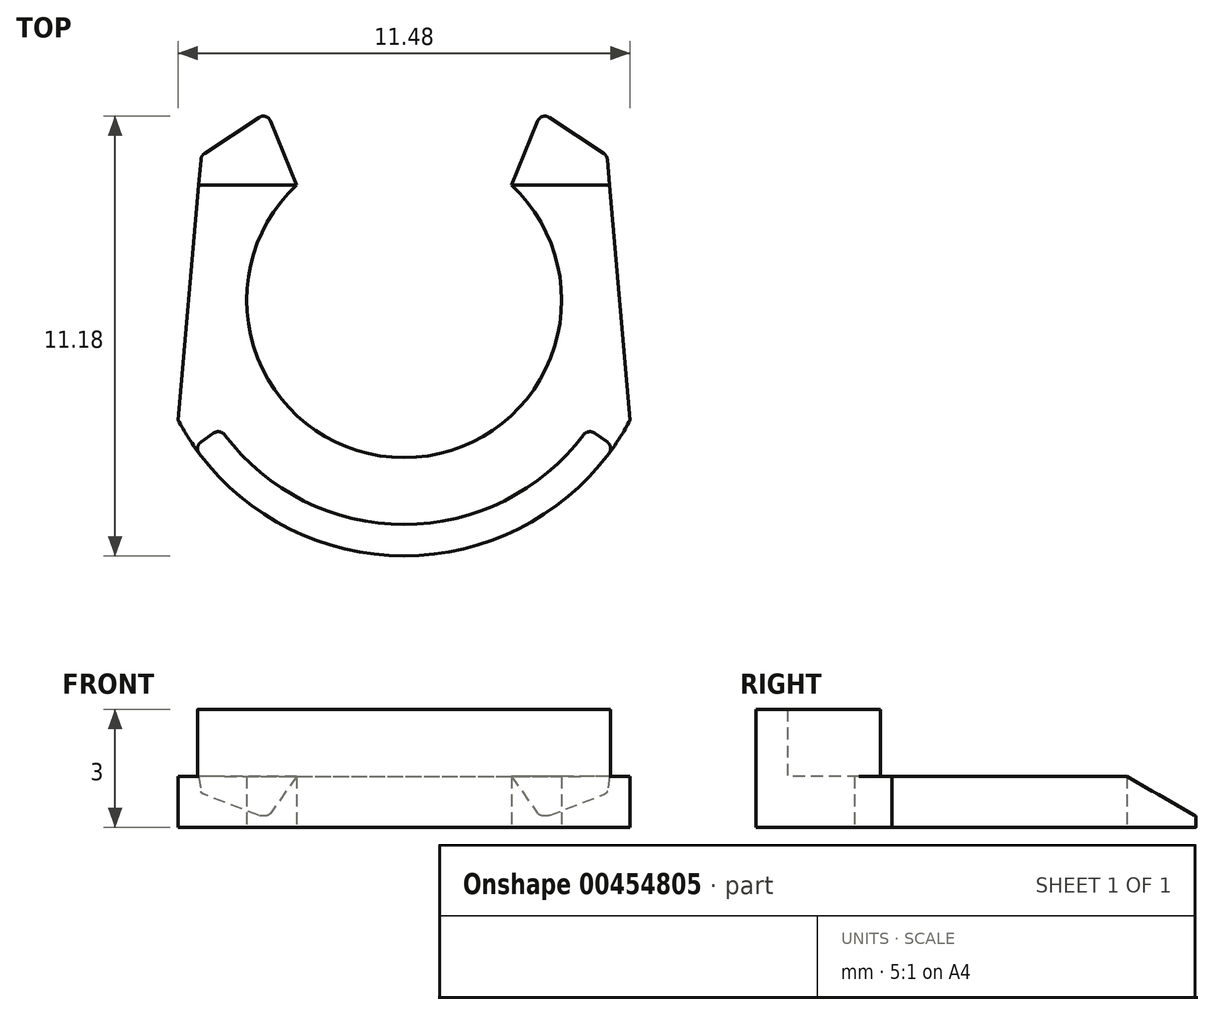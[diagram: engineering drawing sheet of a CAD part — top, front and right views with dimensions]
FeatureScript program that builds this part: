
annotation { "Feature Type Name" : "Feature", "Feature Type Description" : "" }
export const myFeature = defineFeature(function(context is Context, id is Id, definition is map)
    precondition{}
    {
        {
            assignVariable(context, id + "F0", {"name" : "thickness", "anyValue" : 1.3});
        }
        {
            var Q0;
            Q0=qCreatedBy(makeId("Top.planeOp"),FACE);
            var sketch = newSketch(context, id + "F1", { "sketchPlane" : qUnion([Q0])});
            skLineSegment(sketch, "E0.bottom", {"start": v(6, -6) * mm, "end": v(-6, -6) * mm, "construction": true});
            skLineSegment(sketch, "E0.top", {"start": v(4.95, 6) * mm, "end": v(-4.95, 6) * mm, "construction": true});
            skLineSegment(sketch, "E0.left", {"start": v(6, -6) * mm, "end": v(5.74, -3.05) * mm, "construction": true});
            skLineSegment(sketch, "E0.right", {"start": v(-6, -6) * mm, "end": v(-5.74, -3.05) * mm, "construction": true});
            skPoint(sketch, "E0.middle", {"position": v(0, 0) * mm});
            skPoint(sketch, "E1", {"position": v(0, 6) * mm});
            skPoint(sketch, "E2", {"position": v(0, -6) * mm});
            skLineSegment(sketch, "E3", {"start": v(0, 6) * mm, "end": v(0, -6) * mm, "construction": true});
            skLineSegment(sketch, "E4", {"start": v(-5.74, -3.05) * mm, "end": v(-5.15, 3.67) * mm});
            skLineSegment(sketch, "E5", {"start": v(5.74, -3.05) * mm, "end": v(5.15, 3.67) * mm});
            skArc(sketch, "E6", {"start": v(5.74, -3.05) * mm, "mid": v(0, 6.5) * mm, "end": v(-5.74, -3.05) * mm, "construction": true});
            skArc(sketch, "E7", {"start": v(-5.74, -3.05) * mm, "mid": v(0, -6.5) * mm, "end": v(5.74, -3.05) * mm});
            skLineSegment(sketch, "E8", {"start": v(2.73, 2.93) * mm, "end": v(3.49, 4.78) * mm});
            skLineSegment(sketch, "E9", {"start": v(3.49, 4.78) * mm, "end": v(5.15, 3.67) * mm});
            skLineSegment(sketch, "E10", {"start": v(-2.73, 2.93) * mm, "end": v(-3.49, 4.78) * mm});
            skLineSegment(sketch, "E11", {"start": v(-3.49, 4.78) * mm, "end": v(-5.15, 3.67) * mm});
            skLineSegment(sketch, "E12", {"start": v(-5.15, 3.67) * mm, "end": v(-4.95, 6) * mm, "construction": true});
            skLineSegment(sketch, "E13", {"start": v(5.15, 3.67) * mm, "end": v(4.95, 6) * mm, "construction": true});
            skArc(sketch, "E14", {"start": v(2.73, 2.93) * mm, "mid": v(0, 4) * mm, "end": v(-2.73, 2.93) * mm, "construction": true});
            skArc(sketch, "E15", {"start": v(-2.73, 2.93) * mm, "mid": v(0, -4) * mm, "end": v(2.73, 2.93) * mm});
            skSolve(sketch);
        }
        {
            var Q0;
            Q0 = qSketchRegion(id + "F1", true);
            extrude(context, id + "F2", {"entities" : qUnion([Q0]), "depth" : (getVariable(context, 'thickness')) * mm});
        }
        {
            var Q0;
            Q0=makeQuery(id+"F2.opExtrude","CAP_FACE",FACE,{"disambiguationData":[OSD([sQuery(id+"F1.wireOp",EDGE,"E4"),sQuery(id+"F1.wireOp",EDGE,"E5"),sQuery(id+"F1.wireOp",EDGE,"E7"),sQuery(id+"F1.wireOp",EDGE,"E8"),sQuery(id+"F1.wireOp",EDGE,"E9"),sQuery(id+"F1.wireOp",EDGE,"E10"),sQuery(id+"F1.wireOp",EDGE,"E11"),sQuery(id+"F1.wireOp",EDGE,"E15")])],"isStart":false});
            var sketch = newSketch(context, id + "F3", { "sketchPlane" : qUnion([Q0])});
            skArc(sketch, "E16.0", {"start": v(-5.33, -3.72) * mm, "mid": v(0, -6.5) * mm, "end": v(5.33, -3.72) * mm});
            skArc(sketch, "E17", {"start": v(-4.67, -3.27) * mm, "mid": v(0, -5.7) * mm, "end": v(4.67, -3.27) * mm});
            skLineSegment(sketch, "E18", {"start": v(0, 0) * mm, "end": v(-4.67, -3.27) * mm, "construction": true});
            skLineSegment(sketch, "E19", {"start": v(-9.02, -6.3) * mm, "end": v(9.02, -6.3) * mm, "construction": true});
            skLineSegment(sketch, "E20", {"start": v(9.02, -6.3) * mm, "end": v(5.33, -3.72) * mm, "construction": true});
            skLineSegment(sketch, "E21", {"start": v(0, -6.3) * mm, "end": v(0, 0) * mm, "construction": true});
            skLineSegment(sketch, "E22", {"start": v(-5.33, -3.72) * mm, "end": v(-9.02, -6.3) * mm});
            skLineSegment(sketch, "E23", {"start": v(-4.67, -3.27) * mm, "end": v(-5.33, -3.72) * mm});
            skLineSegment(sketch, "E24", {"start": v(5.33, -3.72) * mm, "end": v(4.67, -3.27) * mm});
            skLineSegment(sketch, "E25", {"start": v(4.67, -3.27) * mm, "end": v(0, 0) * mm, "construction": true});
            skPoint(sketch, "E26.orphan", {"position": v(-5.74, -3.05) * mm});
            skPoint(sketch, "E27.orphan", {"position": v(5.74, -3.05) * mm});
            skPoint(sketch, "E28", {"position": v(-5, -3.5) * mm});
            skPoint(sketch, "E29", {"position": v(5, -3.5) * mm});
            skSolve(sketch);
        }
        {
            var Q0;
            Q0 = qSketchRegion(id + "F3", true);
            extrude(context, id + "F4", {"entities" : qUnion([Q0]), "operationType" : NewBodyOperationType.ADD, "depth" : 1.7 * mm});
        }
        {
            var Q0;
            Q0=qCreatedBy(makeId("Right.planeOp"),FACE);
            var sketch = newSketch(context, id + "F5", { "sketchPlane" : qUnion([Q0])});
            skPoint(sketch, "E30.0", {"position": v(2.93, 1.3) * mm});
            skLineSegment(sketch, "E31", {"start": v(2.93, 1.3) * mm, "end": v(6.78, -0.92) * mm});
            skLineSegment(sketch, "E32", {"start": v(6.78, -0.92) * mm, "end": v(6.78, 1.3) * mm});
            skLineSegment(sketch, "E33", {"start": v(6.78, 1.3) * mm, "end": v(2.93, 1.3) * mm});
            skPoint(sketch, "E34.0", {"position": v(4.78, 1.3) * mm});
            skSolve(sketch);
        }
        {
            var Q0;
            Q0 = qSketchRegion(id + "F5", true);
            extrude(context, id + "F6", {"entities" : qUnion([Q0]), "operationType" : NewBodyOperationType.REMOVE, "endBound" : BoundingType.SYMMETRIC, "depth" : 25 * mm});
        }
        {
            var Q0;
            Q0=makeQuery(id+"F4.opExtrude","SWEPT_EDGE",EDGE,{"disambiguationData":[OSD([sQuery(id+"F3.wireOp",EDGE,"E17"),sQuery(id+"F3.wireOp",EDGE,"E24")])]});
            var Q1;
            Q1=makeQuery(id+"F4.opExtrude","SWEPT_EDGE",EDGE,{"disambiguationData":[OSD([sQuery(id+"F1.wireOp",EDGE,"E7"),sQuery(id+"F3.wireOp",EDGE,"E16.0"),sQuery(id+"F3.wireOp",EDGE,"E23")])]});
            var Q2;
            Q2=makeQuery(id+"F4.opExtrude","SWEPT_EDGE",EDGE,{"disambiguationData":[OSD([sQuery(id+"F3.wireOp",EDGE,"E17"),sQuery(id+"F3.wireOp",EDGE,"E23")])]});
            var Q3;
            Q3=makeQuery(id+"F4.opExtrude","SWEPT_EDGE",EDGE,{"disambiguationData":[OSD([sQuery(id+"F1.wireOp",EDGE,"E7"),sQuery(id+"F3.wireOp",EDGE,"E16.0"),sQuery(id+"F3.wireOp",EDGE,"E24")])]});
            var Q4;
            Q4=makeQuery(id+"F2.opExtrude","SWEPT_EDGE",EDGE,{"disambiguationData":[OSD([sQuery(id+"F1.wireOp",EDGE,"E8"),sQuery(id+"F1.wireOp",EDGE,"E9")])]});
            var Q5;
            Q5=makeQuery(id+"F2.opExtrude","SWEPT_EDGE",EDGE,{"disambiguationData":[OSD([sQuery(id+"F1.wireOp",EDGE,"E5"),sQuery(id+"F1.wireOp",EDGE,"E9")])]});
            var Q6;
            Q6=makeQuery(id+"F2.opExtrude","SWEPT_EDGE",EDGE,{"disambiguationData":[OSD([sQuery(id+"F1.wireOp",EDGE,"E10"),sQuery(id+"F1.wireOp",EDGE,"E11")])]});
            var Q7;
            Q7=makeQuery(id+"F2.opExtrude","SWEPT_EDGE",EDGE,{"disambiguationData":[OSD([sQuery(id+"F1.wireOp",EDGE,"E4"),sQuery(id+"F1.wireOp",EDGE,"E11")])]});
            fillet(context, id + "F7", {"entities" : qUnion([Q0, Q1, Q2, Q3, Q4, Q5, Q6, Q7]), "radius" : 0.2 * mm, "tangentPropagation" : true, "allowEdgeOverflow" : false});
        }
    });
